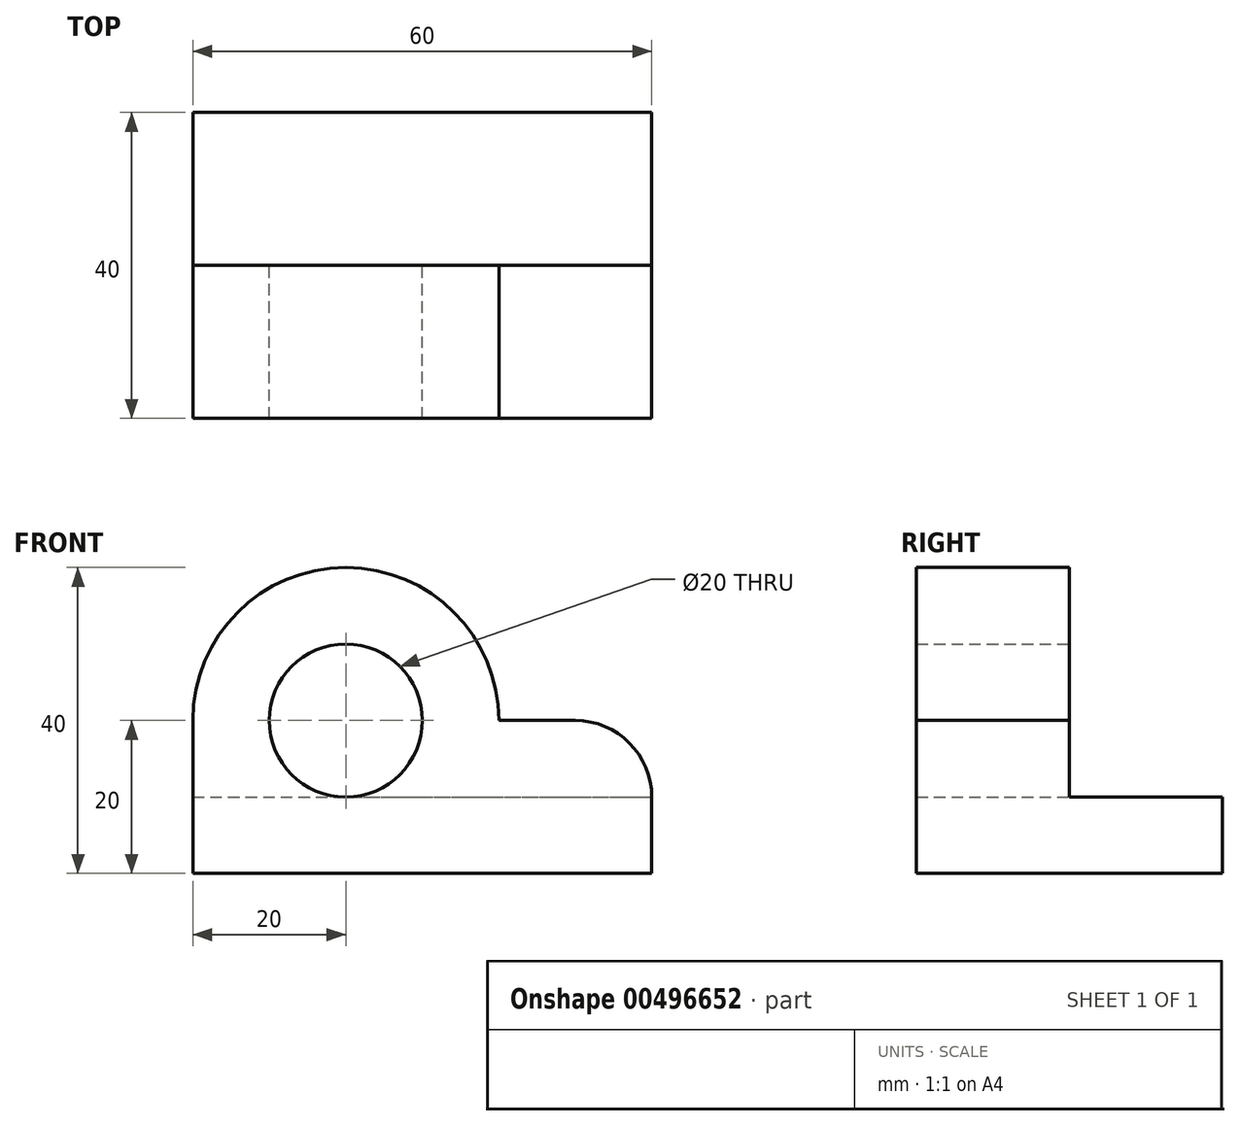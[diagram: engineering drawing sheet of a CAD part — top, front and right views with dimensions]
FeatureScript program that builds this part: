
annotation { "Feature Type Name" : "Feature", "Feature Type Description" : "" }
export const myFeature = defineFeature(function(context is Context, id is Id, definition is map)
    precondition{}
    {
        {
            var Q0;
            Q0=qCreatedBy(makeId("Top.planeOp"),FACE);
            var sketch = newSketch(context, id + "F0", { "sketchPlane" : qUnion([Q0])});
            skLineSegment(sketch, "E0.bottom", {"start": v(0, 0) * mm, "end": v(60, 0) * mm});
            skLineSegment(sketch, "E0.top", {"start": v(0, 40) * mm, "end": v(60, 40) * mm});
            skLineSegment(sketch, "E0.left", {"start": v(0, 0) * mm, "end": v(0, 40) * mm});
            skLineSegment(sketch, "E0.right", {"start": v(60, 0) * mm, "end": v(60, 40) * mm});
            skSolve(sketch);
        }
        {
            var Q0;
            Q0 = qSketchRegion(id + "F0", true);
            extrude(context, id + "F1", {"entities" : qUnion([Q0]), "depth" : 10 * mm});
        }
        {
            var Q0;
            Q0=makeQuery(id+"F1.opExtrude","SWEPT_FACE",FACE,{"disambiguationData":[OSD([sQuery(id+"F0.wireOp",EDGE,"E0.bottom")])]});
            var sketch = newSketch(context, id + "F2", { "sketchPlane" : qUnion([Q0])});
            skPoint(sketch, "E1", {"position": v(20, 20) * mm});
            skArc(sketch, "E2", {"start": v(40, 20) * mm, "mid": v(20, 40) * mm, "end": v(0, 20) * mm});
            skLineSegment(sketch, "E3", {"start": v(0, 20) * mm, "end": v(0, 10) * mm});
            skLineSegment(sketch, "E4", {"start": v(40, 20) * mm, "end": v(50, 20) * mm});
            skLineSegment(sketch, "E5", {"start": v(60, 10) * mm, "end": v(60, 10) * mm});
            skPoint(sketch, "E6.visualSharp", {"position": v(60, 20) * mm});
            skArc(sketch, "E6.filletArc", {"start": v(60, 10) * mm, "mid": v(57.07, 17.07) * mm, "end": v(50, 20) * mm});
            skLineSegment(sketch, "E7", {"start": v(0, 10) * mm, "end": v(60, 10) * mm});
            skSolve(sketch);
        }
        {
            var Q0;
            Q0 = qSketchRegion(id + "F2", true);
            extrude(context, id + "F3", {"entities" : qUnion([Q0]), "operationType" : NewBodyOperationType.ADD, "oppositeDirection" : true, "depth" : 20 * mm});
        }
        {
            var Q0;
            Q0=makeQuery(id+"F3.opExtrude","CAP_FACE",FACE,{"disambiguationData":[OSD([sQuery(id+"F2.wireOp",EDGE,"E2"),sQuery(id+"F2.wireOp",EDGE,"E3"),sQuery(id+"F2.wireOp",EDGE,"E4"),sQuery(id+"F2.wireOp",EDGE,"E6.filletArc"),sQuery(id+"F2.wireOp",EDGE,"E7")])],"isStart":false});
            var sketch = newSketch(context, id + "F4", { "sketchPlane" : qUnion([Q0])});
            skCircle(sketch, "E8", {"center": v(-20, 20) * mm, "radius": 10 * mm});
            skSolve(sketch);
        }
        {
            var Q0;
            Q0 = qSketchRegion(id + "F4", true);
            extrude(context, id + "F5", {"entities" : qUnion([Q0]), "operationType" : NewBodyOperationType.REMOVE, "oppositeDirection" : true, "depth" : 25 * mm});
        }
    });
